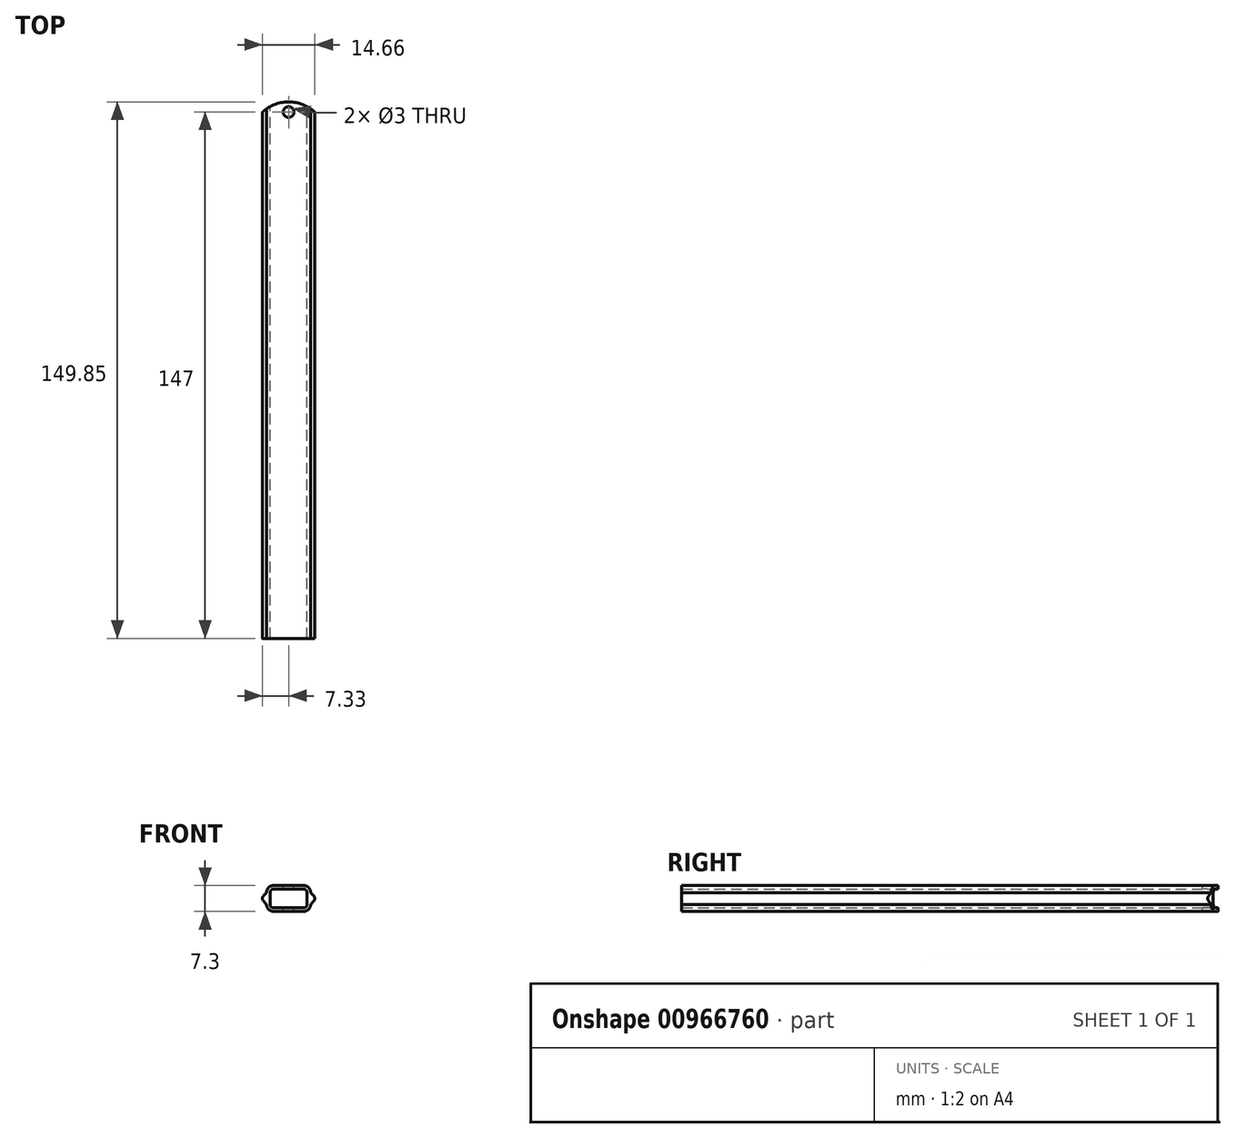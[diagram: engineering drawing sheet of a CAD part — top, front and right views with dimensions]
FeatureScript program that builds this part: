
annotation { "Feature Type Name" : "Feature", "Feature Type Description" : "" }
export const myFeature = defineFeature(function(context is Context, id is Id, definition is map)
    precondition{}
    {
        {
            var Q0;
            Q0=qCreatedBy(makeId("Front.planeOp"),FACE);
            var sketch = newSketch(context, id + "F0", { "sketchPlane" : qUnion([Q0])});
            skLineSegment(sketch, "E0.bottom", {"start": v(4.15, -2.65) * mm, "end": v(-4.15, -2.65) * mm});
            skLineSegment(sketch, "E0.top", {"start": v(4.15, 2.65) * mm, "end": v(-4.15, 2.65) * mm});
            skLineSegment(sketch, "E0.left", {"start": v(5.15, -1.65) * mm, "end": v(5.15, 1.65) * mm});
            skLineSegment(sketch, "E0.right", {"start": v(-5.15, -1.65) * mm, "end": v(-5.15, 1.65) * mm});
            skPoint(sketch, "E0.middle", {"position": v(0, 0) * mm});
            skPoint(sketch, "E1.visualSharp", {"position": v(-5.15, 2.65) * mm});
            skArc(sketch, "E1.filletArc", {"start": v(-4.15, 2.65) * mm, "mid": v(-4.86, 2.36) * mm, "end": v(-5.15, 1.65) * mm});
            skPoint(sketch, "E2.visualSharp", {"position": v(5.15, 2.65) * mm});
            skArc(sketch, "E2.filletArc", {"start": v(5.15, 1.65) * mm, "mid": v(4.86, 2.36) * mm, "end": v(4.15, 2.65) * mm});
            skPoint(sketch, "E3.visualSharp", {"position": v(5.15, -2.65) * mm});
            skArc(sketch, "E3.filletArc", {"start": v(4.15, -2.65) * mm, "mid": v(4.86, -2.36) * mm, "end": v(5.15, -1.65) * mm});
            skPoint(sketch, "E4.visualSharp", {"position": v(-5.15, -2.65) * mm});
            skArc(sketch, "E4.filletArc", {"start": v(-5.15, -1.65) * mm, "mid": v(-4.86, -2.36) * mm, "end": v(-4.15, -2.65) * mm});
            skArc(sketch, "E5.0", {"start": v(6.15, 1.65) * mm, "mid": v(5.56, 3.06) * mm, "end": v(4.15, 3.65) * mm});
            skLineSegment(sketch, "E5.2", {"start": v(4.15, 3.65) * mm, "end": v(-4.15, 3.65) * mm});
            skArc(sketch, "E5.3", {"start": v(4.15, -3.65) * mm, "mid": v(5.56, -3.06) * mm, "end": v(6.15, -1.65) * mm});
            skArc(sketch, "E5.4", {"start": v(-4.15, 3.65) * mm, "mid": v(-5.56, 3.06) * mm, "end": v(-6.15, 1.65) * mm});
            skArc(sketch, "E5.6", {"start": v(-6.15, -1.65) * mm, "mid": v(-5.56, -3.06) * mm, "end": v(-4.15, -3.65) * mm});
            skLineSegment(sketch, "E5.7", {"start": v(4.15, -3.65) * mm, "end": v(-4.15, -3.65) * mm});
            skLineSegment(sketch, "E6", {"start": v(-7.06, 0.69) * mm, "end": v(-6.15, 1.65) * mm});
            skLineSegment(sketch, "E7.MirrorCS", {"start": v(-7.06, -0.69) * mm, "end": v(-6.15, -1.65) * mm});
            skLineSegment(sketch, "E8.MirrorCS", {"start": v(7.06, 0.69) * mm, "end": v(6.15, 1.65) * mm});
            skLineSegment(sketch, "E9.MirrorCS", {"start": v(7.06, -0.69) * mm, "end": v(6.15, -1.65) * mm});
            skPoint(sketch, "E10.visualSharp", {"position": v(-7.7, 0) * mm});
            skArc(sketch, "E10.filletArc", {"start": v(-7.06, 0.69) * mm, "mid": v(-7.33, 0) * mm, "end": v(-7.06, -0.69) * mm});
            skPoint(sketch, "E11.visualSharp", {"position": v(7.7, 0) * mm});
            skArc(sketch, "E11.filletArc", {"start": v(7.06, -0.69) * mm, "mid": v(7.33, 0) * mm, "end": v(7.06, 0.69) * mm});
            skSolve(sketch);
        }
        {
            var Q0;
            Q0=makeQuery(id+"F0.imprint","IMPRINT",FACE,{"disambiguationData":[TD([[makeQuery(id+"F0.imprint","IMPRINT",EDGE,{"derivedFrom":sQuery(id+"F0.wireOp",EDGE,"E0.bottom")}),1.0]])]});
            extrude(context, id + "F1", {"entities" : qUnion([Q0]), "depth" : 150 * mm, "offsetDistance" : 25 * mm});
        }
        {
            var Q0;
            Q0=makeQuery(id+"F1.opExtrude","SWEPT_FACE",FACE,{"disambiguationData":[OSD([sQuery(id+"F0.wireOp",EDGE,"E5.2")])]});
            var sketch = newSketch(context, id + "F2", { "sketchPlane" : qUnion([Q0])});
            skCircle(sketch, "E12", {"center": v(0, -3) * mm, "radius": 1.5 * mm});
            skSolve(sketch);
        }
        {
            var Q0;
            Q0=makeQuery(id+"F2.imprint","IMPRINT",FACE,{"disambiguationData":[TD([[makeQuery(id+"F2.imprint","IMPRINT",EDGE,{"derivedFrom":sQuery(id+"F2.wireOp",EDGE,"S33YdpTx-NKYe-flyp-kQUo-xBa4HNO2xXOk")}),1.0]])]});
            var Q1;
            Q1=makeQuery(id+"F2.imprint","IMPRINT",FACE,{"disambiguationData":[TD([[makeQuery(id+"F2.imprint","IMPRINT",EDGE,{"derivedFrom":sQuery(id+"F2.wireOp",EDGE,"E12")}),1.0]])]});
            extrude(context, id + "F3", {"entities" : qUnion([Q0, Q1]), "operationType" : NewBodyOperationType.REMOVE, "endBound" : BoundingType.THROUGH_ALL, "oppositeDirection" : true, "depth" : 25 * mm, "offsetDistance" : 25 * mm});
        }
        {
            var Q0;
            Q0=qCreatedBy(makeId("Top.planeOp"),FACE);
            cPlane(context, id + "F4", {"entities" : qUnion([Q0]), "cplaneType" : CPlaneType.OFFSET, "offset" : 4.6 * mm, "width" : 150 * mm, "height" : 150 * mm});
        }
        {
            var Q0;
            Q0=qCreatedBy(id+"F4.planeOp",FACE);
            var sketch = newSketch(context, id + "F5", { "sketchPlane" : qUnion([Q0])});
            skLineSegment(sketch, "E13.bottom", {"start": v(8, 3.7) * mm, "end": v(-8, 3.7) * mm});
            skLineSegment(sketch, "E13.left", {"start": v(8, 3.7) * mm, "end": v(8, -3.7) * mm});
            skLineSegment(sketch, "E13.right", {"start": v(-8, 3.7) * mm, "end": v(-8, -3.7) * mm});
            skPoint(sketch, "E13.middle", {"position": v(0, 0) * mm});
            skArc(sketch, "E14", {"start": v(8, -3.7) * mm, "mid": v(0, -0.15) * mm, "end": v(-8, -3.7) * mm});
            skSolve(sketch);
        }
        {
            var Q0;
            Q0=makeQuery(id+"F5.imprint","IMPRINT",FACE,{"disambiguationData":[TD([[makeQuery(id+"F5.imprint","IMPRINT",EDGE,{"derivedFrom":sQuery(id+"F5.wireOp",EDGE,"E13.bottom")}),1.0]])]});
            extrude(context, id + "F6", {"entities" : qUnion([Q0]), "operationType" : NewBodyOperationType.REMOVE, "oppositeDirection" : true, "depth" : 25 * mm, "offsetDistance" : 25 * mm});
        }
    });
